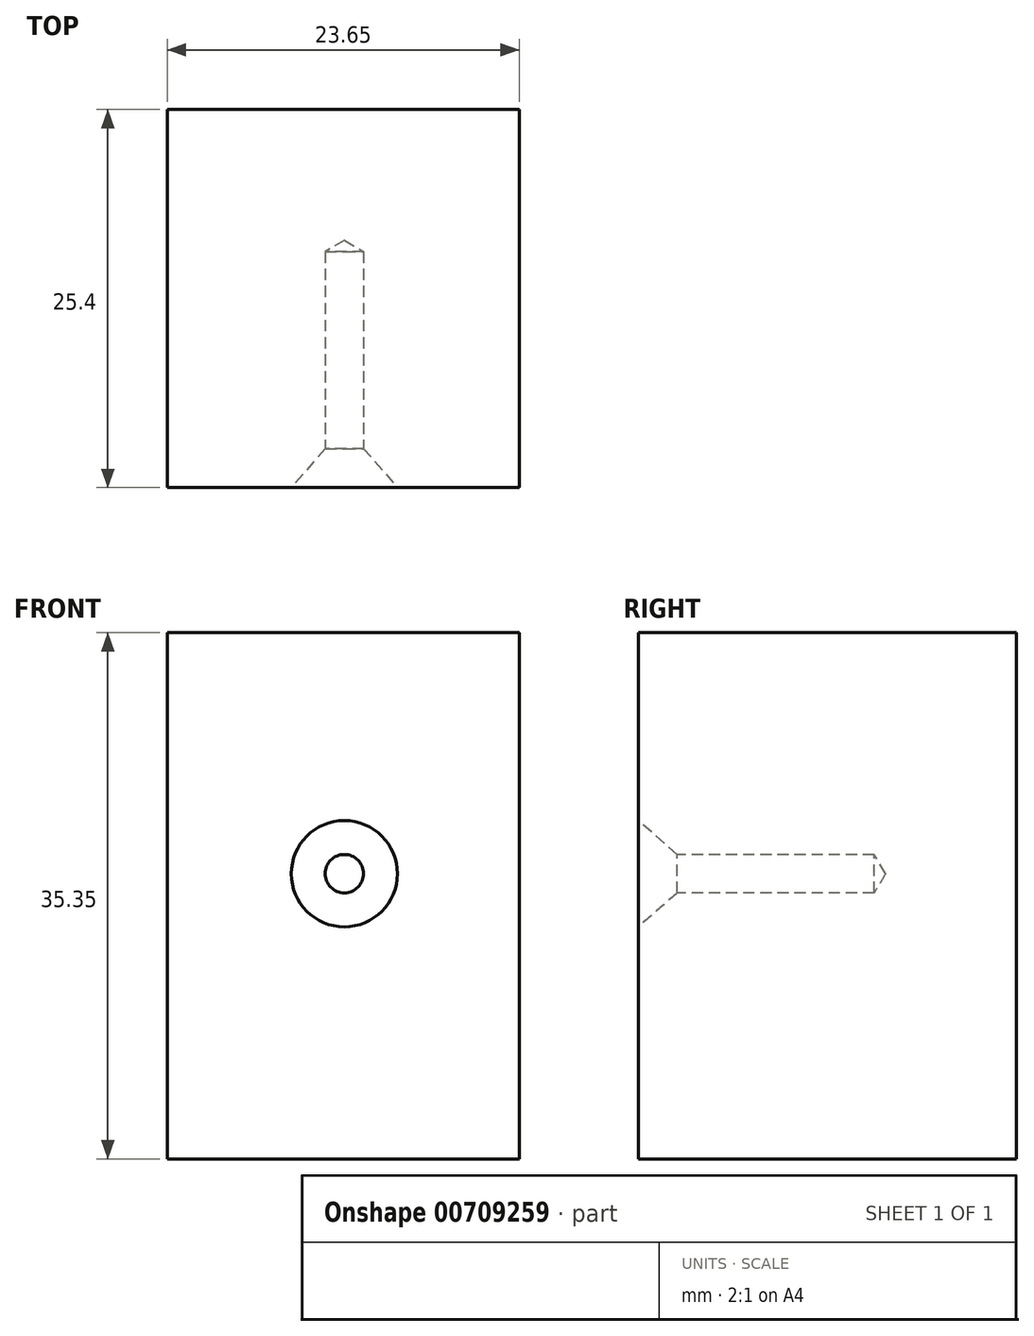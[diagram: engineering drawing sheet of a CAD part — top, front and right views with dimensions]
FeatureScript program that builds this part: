
annotation { "Feature Type Name" : "Feature", "Feature Type Description" : "" }
export const myFeature = defineFeature(function(context is Context, id is Id, definition is map)
    precondition{}
    {
        {
            var Q0;
            Q0=qCreatedBy(makeId("Front.planeOp"),FACE);
            var sketch = newSketch(context, id + "F0", { "sketchPlane" : qUnion([Q0])});
            skLineSegment(sketch, "E0.bottom", {"start": v(-69, 63.86) * mm, "end": v(-45.34, 63.86) * mm});
            skLineSegment(sketch, "E0.top", {"start": v(-69, 28.5) * mm, "end": v(-45.34, 28.5) * mm});
            skLineSegment(sketch, "E0.left", {"start": v(-69, 63.86) * mm, "end": v(-69, 28.5) * mm});
            skLineSegment(sketch, "E0.right", {"start": v(-45.34, 63.86) * mm, "end": v(-45.34, 28.5) * mm});
            skSolve(sketch);
        }
        {
            var Q0;
            Q0 = qSketchRegion(id + "F0", true);
            extrude(context, id + "F1", {"entities" : qUnion([Q0]), "depth" : 25.4 * mm, "offsetDistance" : 25.4 * mm});
        }
        {
            var Q0;
            Q0=makeQuery(id+"F1.opExtrude","CAP_FACE",FACE,{"disambiguationData":[OSD([sQuery(id+"F0.wireOp",EDGE,"E0.bottom"),sQuery(id+"F0.wireOp",EDGE,"E0.top"),sQuery(id+"F0.wireOp",EDGE,"E0.left"),sQuery(id+"F0.wireOp",EDGE,"E0.right")])],"isStart":false});
            var sketch = newSketch(context, id + "F2", { "sketchPlane" : qUnion([Q0])});
            skPoint(sketch, "E1", {"position": v(-57.09, 47.67) * mm});
            skSolve(sketch);
        }
        {
            var Q0;
            Q0=sQuery(id+"F2.wireOp",VERTEX,"E1");
            var Q1;
            Q1=makeQuery(id+"F1.opExtrude","SWEPT_BODY",BODY,{"disambiguationData":[OSD([sQuery(id+"F0.wireOp",EDGE,"E0.bottom"),sQuery(id+"F0.wireOp",EDGE,"E0.top"),sQuery(id+"F0.wireOp",EDGE,"E0.left"),sQuery(id+"F0.wireOp",EDGE,"E0.right")])]});
            hole(context, id + "F3", {"style" : HoleStyle.C_SINK, "endStyle" : HoleEndStyle.BLIND, "standardTappedOrClearance" : lookupTablePath({ "standard" : "ANSI", "engagement" : "75%", "pitch" : "40 tpi", "size" : "#5", "type" : "Tapped" }), "standardBlindInLast" : lookupTablePath({ "standard" : "ANSI", "engagement" : "75%", "pitch" : "40 tpi", "size" : "#5", "type" : "Tapped" }), "holeDiameter" : 2.58 * mm, "cSinkDiameter" : 7.14 * mm, "cSinkAngle" : 82 * degree, "majorDiameter" : 3.17 * mm, "showTappedDepth" : true, "holeDepth" : 15.85 * mm, "isTappedThrough" : true, "tappedDepth" : 13.94 * mm, "tapClearance" : 3, "locations" : qUnion([Q0]), "scope" : qUnion([Q1])});
        }
    });
